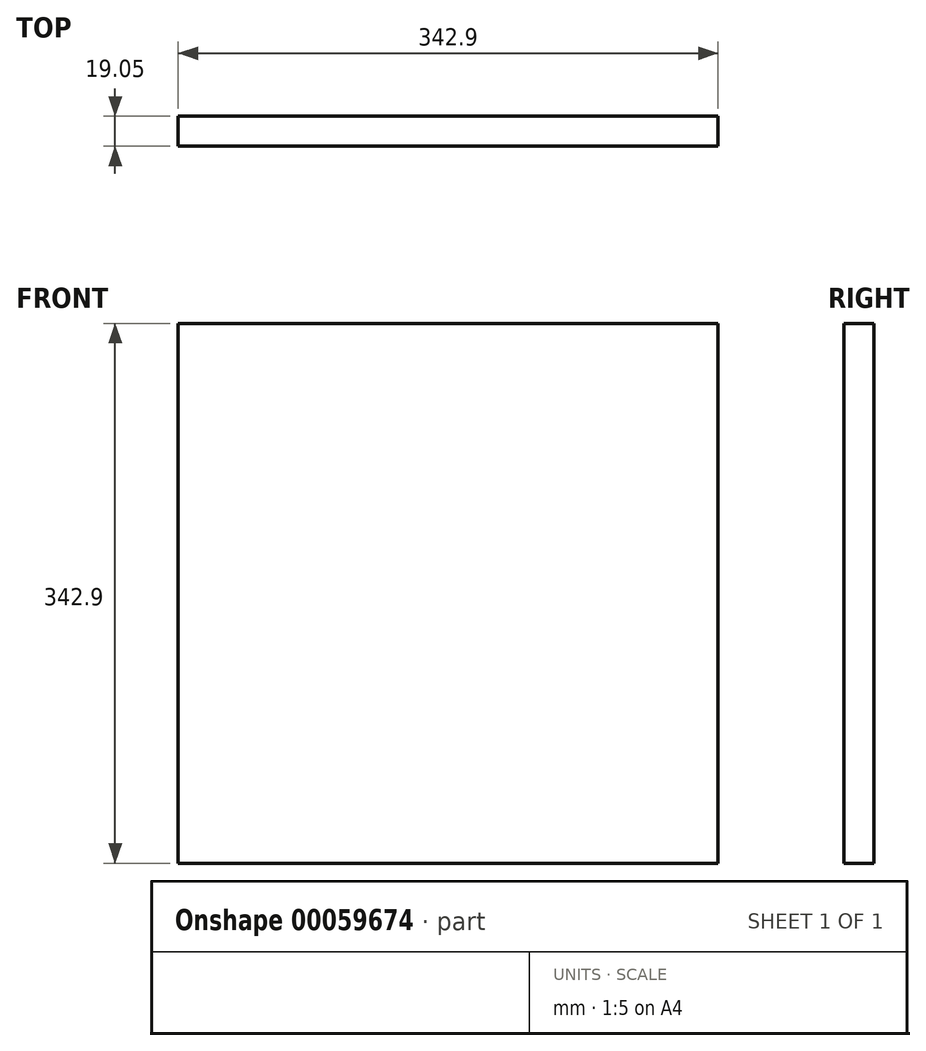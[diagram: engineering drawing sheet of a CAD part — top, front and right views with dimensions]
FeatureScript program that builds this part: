
annotation { "Feature Type Name" : "Feature", "Feature Type Description" : "" }
export const myFeature = defineFeature(function(context is Context, id is Id, definition is map)
    precondition{}
    {
        {
            var Q0;
            Q0=qCreatedBy(makeId("Front.planeOp"),FACE);
            var sketch = newSketch(context, id + "F0", { "sketchPlane" : qUnion([Q0])});
            skLineSegment(sketch, "E0.bottom", {"start": v(0, 0) * mm, "end": v(342.9, 0) * mm});
            skLineSegment(sketch, "E0.top", {"start": v(0, 342.9) * mm, "end": v(342.9, 342.9) * mm});
            skLineSegment(sketch, "E0.left", {"start": v(0, 0) * mm, "end": v(0, 342.9) * mm});
            skLineSegment(sketch, "E0.right", {"start": v(342.9, 0) * mm, "end": v(342.9, 342.9) * mm});
            skSolve(sketch);
        }
        {
            var Q0;
            Q0=makeQuery(id+"F0.imprint","IMPRINT",FACE,{"disambiguationData":[TD([[makeQuery(id+"F0.imprint","IMPRINT",EDGE,{"derivedFrom":sQuery(id+"F0.wireOp",EDGE,"E0.bottom")}),1.0]])]});
            extrude(context, id + "F1", {"entities" : qUnion([Q0]), "depth" : 19.05 * mm});
        }
    });
